# Revit family: IEK_Выключатель_Встраиваемый_10А одноклавишный кнопочный IP20_КВАРТА
name_source: partatom
category: Выключатели
units: mm (PartAtom-declared; Revit-internal decimal feet)

## family parameters
Всегда вертикально = Да
На основе рабочей плоскости = Нет
Общий = Нет
При загрузке вырезать с полостями = Нет
Размер круглого соединителя = Использовать диаметр
Сохранять ориентацию аннотаций = Да
Тип детали = Нормальный
Точка расчета площади = Нет

## types (2) — shared parameters
ADSK_URL страницы изделия = https://www.iek.ru
ADSK_Версия Revit = 2019
ADSK_Версия семейства = 1.0
ADSK_Группирование = III ЭЛЕКТРОУСТАНОВОЧНЫЕ И ЭЛЕКТРОМОНТАЖНЫЕ ИЗДЕЛИЯ
ADSK_Единица измерения = шт
ADSK_Завод-изготовитель = IEK
ADSK_Количество фаз = 1
ADSK_Количество фаз числовое = 1
ADSK_Марка = КВАРТА
ADSK_Материал наименование = Пластик
ADSK_Напряжение = 220 В
IEK_URL = https://www.iek.ru
IEK_Описание = Классический дизайн, проверенный временем и востребованный различными категориями потребителей, позволяет устанавливать изделия серии "КВАРТА" в квартирах, загородных домах, офисных и производственных помещениях.
IEK_Цена за единицу = 139.9
KSI_CMa_Строительные материалы = 01.7.14.03
KSI_CPr_Строительные изделия = 20.4.01
Высота = 81 мм
Глубина = 46 мм
Изготовитель = IEK
Степень защиты = IP20
Тип монтажа = Скрытый монтаж (в штукатурку)
Ширина = 82 мм

## per-type parameters (varying)
| type | ADSK_Код изделия | ADSK_Масса | ADSK_Материал | ADSK_Наименование |
| ВСк10-1-0-КБ | EVK13-K01-10-DM | 0.09 | Цвет белый | Выключатель 1-клавишный кнопочный звонок ВСк10-1-0-КБ 10А КВАРТА белый IEK |
| ВСк10-1-0-ККм | EVK13-K33-10-DM | 0.087 | Цвет кремовый | Выключатель 1-клавишный кнопочный звонок ВСк10-1-0-ККм 10А КВАРТА кремовый IEK |
